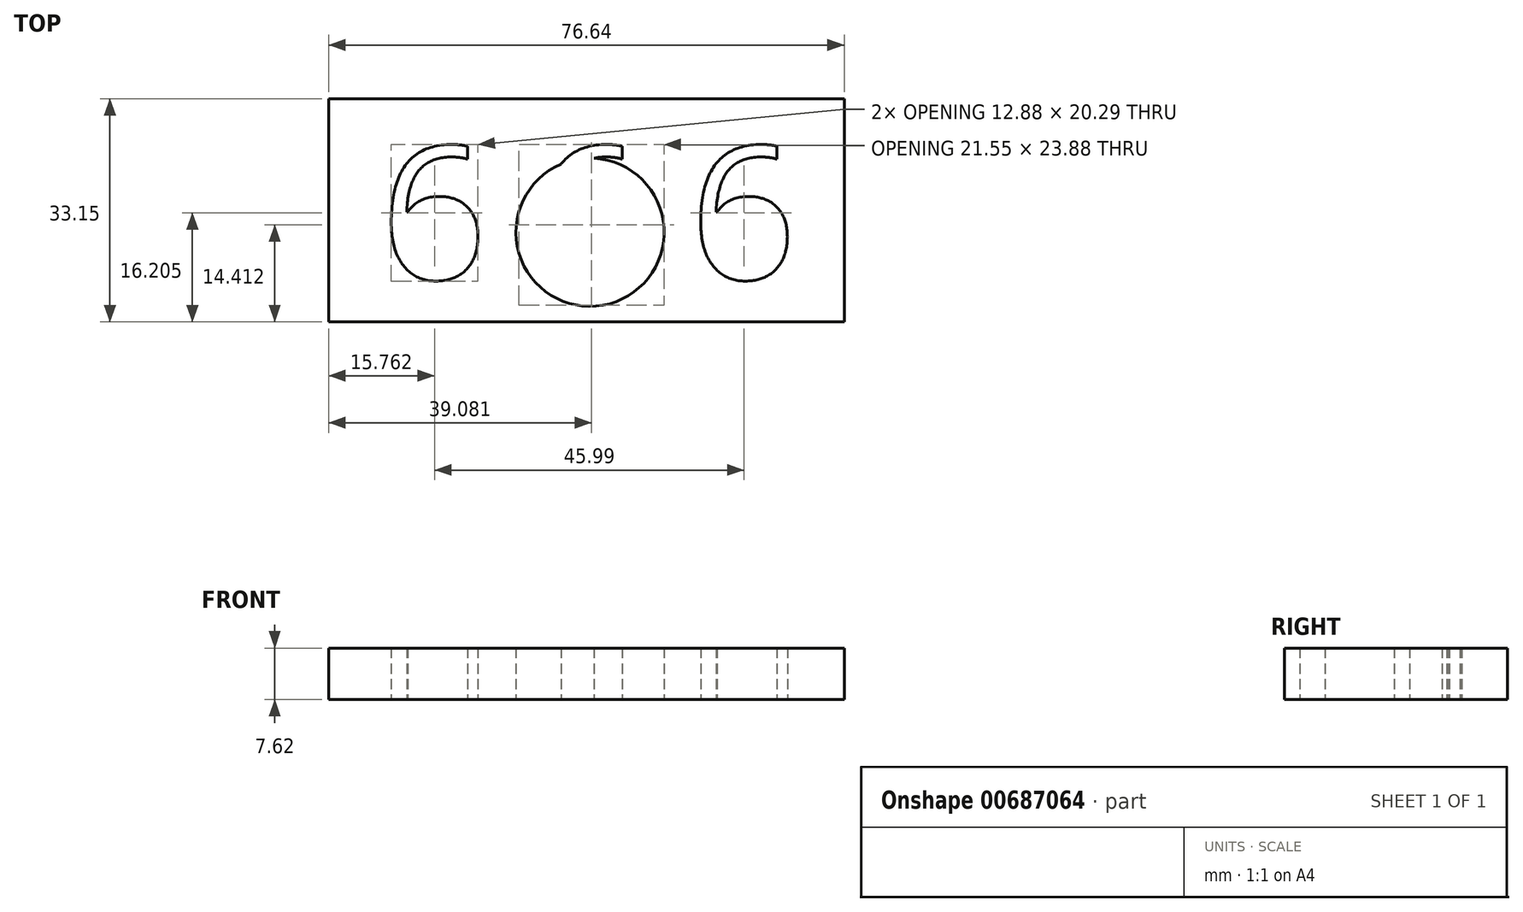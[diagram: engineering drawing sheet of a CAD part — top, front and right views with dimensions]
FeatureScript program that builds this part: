
annotation { "Feature Type Name" : "Feature", "Feature Type Description" : "" }
export const myFeature = defineFeature(function(context is Context, id is Id, definition is map)
    precondition{}
    {
        {
            var Q0;
            Q0=qCreatedBy(makeId("Top.planeOp"),FACE);
            var sketch = newSketch(context, id + "F0", { "sketchPlane" : qUnion([Q0])});
            skLineSegment(sketch, "E0.bottom", {"start": v(-27.42, 16.76) * mm, "end": v(24.36, 16.76) * mm});
            skLineSegment(sketch, "E0.top", {"start": v(-27.42, -16.39) * mm, "end": v(24.36, -16.39) * mm});
            skLineSegment(sketch, "E0.left", {"start": v(-27.42, 16.76) * mm, "end": v(-27.42, -16.39) * mm});
            skText(sketch, "E1", { "text": "6 6 6", "fontName": "OpenSans-Regular.ttf"});
            skLineSegment(sketch, "E2", {"start": v(24.36, 16.76) * mm, "end": v(49.22, 16.76) * mm});
            skLineSegment(sketch, "E3", {"start": v(49.22, 16.76) * mm, "end": v(49.22, -16.39) * mm});
            skLineSegment(sketch, "E4", {"start": v(49.22, -16.39) * mm, "end": v(24.36, -16.39) * mm});
            skCircle(sketch, "E5", {"center": v(11.45, -3.07) * mm, "radius": 11.01 * mm});
            const initialGuessF0  = {"E1": [-0.01968, -0.01006, 1, 0, 0.01991]};
            skSetInitialGuess(sketch, initialGuessF0);
            skSolve(sketch);
        }
        {
            var Q0;
            Q0 = qSketchRegion(id + "F0", true);
            extrude(context, id + "F1", {"entities" : qUnion([Q0]), "depth" : 7.62 * mm, "offsetDistance" : 25.4 * mm});
        }
    });
